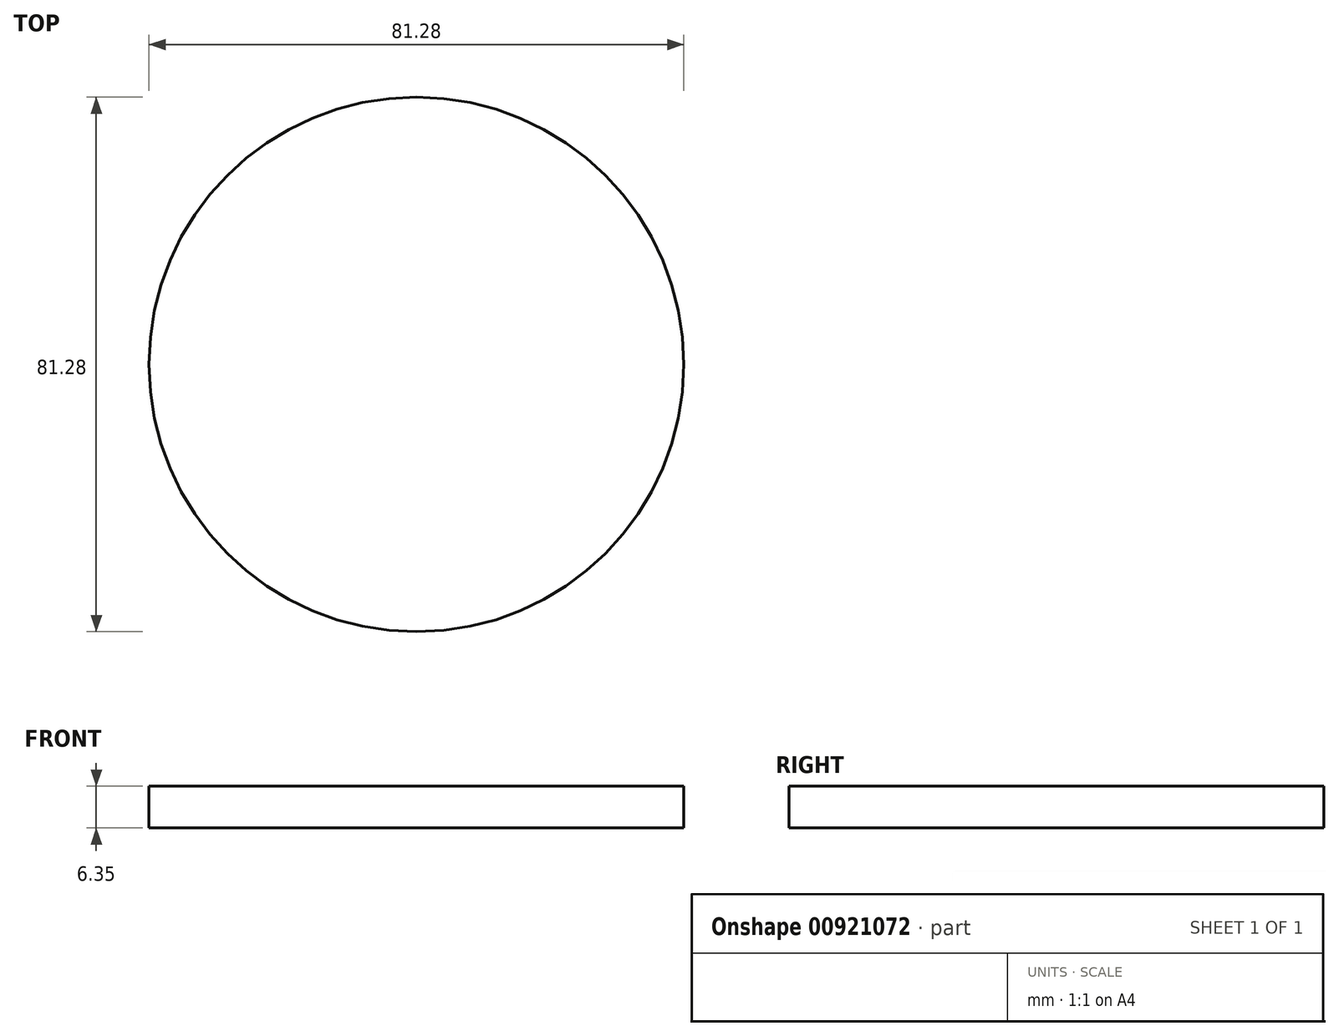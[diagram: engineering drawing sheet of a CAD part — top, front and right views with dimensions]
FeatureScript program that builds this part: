
annotation { "Feature Type Name" : "Feature", "Feature Type Description" : "" }
export const myFeature = defineFeature(function(context is Context, id is Id, definition is map)
    precondition{}
    {
        {
            var Q0;
            Q0=qCreatedBy(makeId("Top.planeOp"),FACE);
            var sketch = newSketch(context, id + "F0", { "sketchPlane" : qUnion([Q0])});
            skCircle(sketch, "E0", {"center": v(0, 0) * mm, "radius": 40.64 * mm});
            skSolve(sketch);
        }
        {
            var Q0;
            Q0 = qSketchRegion(id + "F0", true);
            extrude(context, id + "F1", {"entities" : qUnion([Q0]), "depth" : 6.35 * mm, "offsetDistance" : 25.4 * mm});
        }
    });
